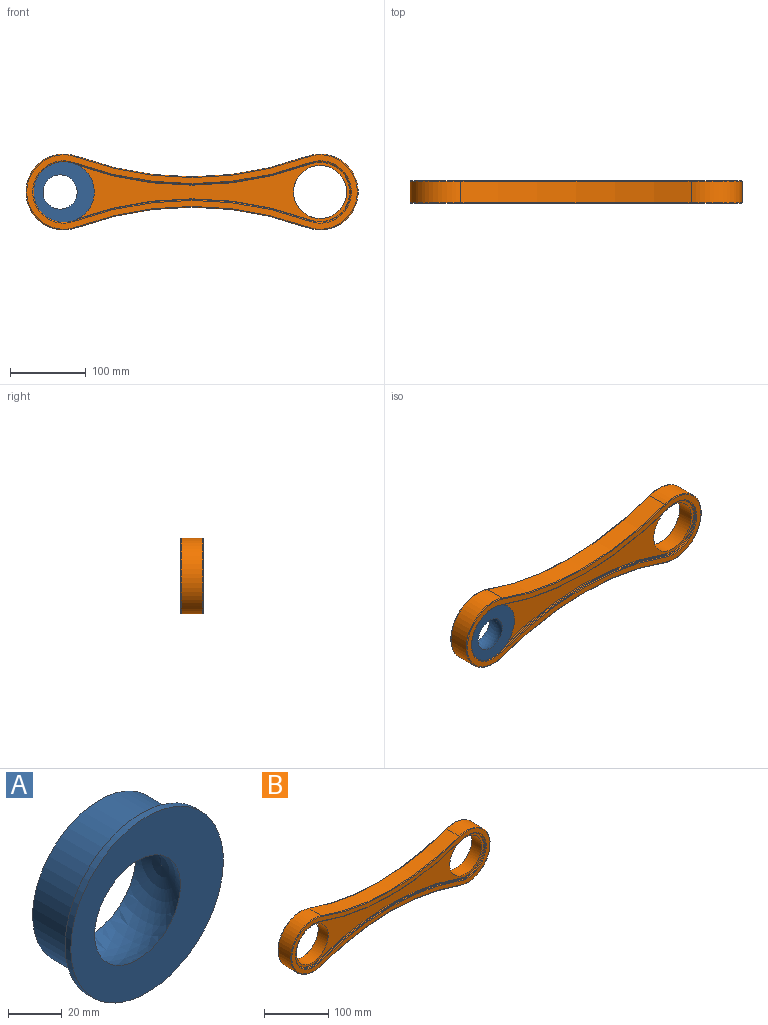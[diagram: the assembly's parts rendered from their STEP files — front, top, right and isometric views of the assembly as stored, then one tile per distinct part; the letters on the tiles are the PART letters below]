
ASSEMBLY  parts=2 mates=1
PART A: 6 faces, bbox 80x53x80 mm
  f0: plane 70x70mm, normal (0,1,0), area 2022.4mm2, adj f1,f5
  f1: cylinder r=35mm len=70mm, axis (0,1,0), area 4838.1mm2, adj f0,f2
  f2: plane 80x80mm, normal (0,1,0), area 1178.1mm2, adj f1,f3
  f3: cylinder r=40mm len=80mm, axis (0,1,0), area 754mm2, adj f2,f4
  f4: plane 80x80mm, normal (0,-1,0), area 3436.1mm2, adj f3,f5
  f5: sphere r=26.5mm, area 4163.4mm2, adj f0,f4
PART B: 42 faces, bbox 445.7x30x108.2 mm
  f0: cylinder r=35mm len=70mm, axis (0,1,0), area 4838.1mm2, adj f12,f17
  f1: cylinder r=35mm len=70mm, axis (0,1,0), area 4838.1mm2, adj f12,f17
  f2: plane 435.5x98mm, normal (0,1,0), area 7775mm2, adj f26,f27,f28,f29,f34,f35,f36,f37
  f3: plane 435.5x98mm, normal (0,-1,0), area 7775mm2, adj f30,f31,f32,f33,f38,f39,f40,f41
  f4: cylinder r=439.61mm len=303.03mm, axis (0,1,0), area 8662.6mm2, adj f5,f7,f36,f40
  f5: cylinder r=50mm len=100mm, axis (0,1,0), area 5383.5mm2, adj f4,f6,f34,f38
  f6: cylinder r=439.61mm len=303.03mm, axis (0,1,0), area 8662.6mm2, adj f5,f7,f35,f39
  f7: cylinder r=50mm len=100mm, axis (0,1,0), area 5383.5mm2, adj f4,f6,f37,f41
  f8: cylinder r=449.61mm len=309.93mm, axis (0,-1,0), area 632.8mm2, adj f9,f11,f24,f30
  f9: cylinder r=40mm len=80mm, axis (0,-1,0), area 307.6mm2, adj f8,f10,f22,f31
  f10: cylinder r=449.61mm len=309.93mm, axis (0,-1,0), area 632.8mm2, adj f9,f11,f23,f33
  f11: cylinder r=40mm len=80mm, axis (0,-1,0), area 307.6mm2, adj f8,f10,f25,f32
  f12: plane 415.5x78mm, normal (0,-1,0), area 10372.7mm2, adj f0,f1,f22,f23,f24,f25
  f13: cylinder r=449.61mm len=309.93mm, axis (0,1,0), area 632.8mm2, adj f14,f16,f20,f26
  f14: cylinder r=40mm len=80mm, axis (0,1,0), area 307.6mm2, adj f13,f15,f21,f28
  f15: cylinder r=449.61mm len=309.93mm, axis (0,1,0), area 632.8mm2, adj f14,f16,f19,f29
  f16: cylinder r=40mm len=80mm, axis (0,1,0), area 307.6mm2, adj f13,f15,f18,f27
  f17: plane 415.5x78mm, normal (0,1,0), area 10372.7mm2, adj f0,f1,f18,f19,f20,f21
  f18: torus R=39mm, axis (0,1,0), area 239.4mm2, adj f16,f17,f19,f20
  f19: torus R=450.61mm, axis (0,1,0), area 497.4mm2, adj f15,f17,f18,f21
  f20: torus R=450.61mm, axis (0,1,0), area 497.4mm2, adj f13,f17,f18,f21
  f21: torus R=39mm, axis (0,1,0), area 239.4mm2, adj f14,f17,f19,f20
  f22: torus R=39mm, axis (0,-1,0), area 239.4mm2, adj f9,f12,f23,f24
  f23: torus R=450.61mm, axis (0,-1,0), area 497.4mm2, adj f10,f12,f22,f25
  f24: torus R=450.61mm, axis (0,-1,0), area 497.4mm2, adj f8,f12,f22,f25
  f25: torus R=39mm, axis (0,-1,0), area 239.4mm2, adj f11,f12,f23,f24
  f26: torus R=448.61mm, axis (0,-1,0), area 496.6mm2, adj f2,f13,f27,f28
  f27: torus R=41mm, axis (0,-1,0), area 243.8mm2, adj f2,f16,f26,f29
  f28: torus R=41mm, axis (0,-1,0), area 243.8mm2, adj f2,f14,f26,f29
  f29: torus R=448.61mm, axis (0,-1,0), area 496.6mm2, adj f2,f15,f27,f28
  f30: torus R=448.61mm, axis (0,-1,0), area 496.6mm2, adj f3,f8,f31,f32
  f31: torus R=41mm, axis (0,-1,0), area 243.8mm2, adj f3,f9,f30,f33
  f32: torus R=41mm, axis (0,-1,0), area 243.8mm2, adj f3,f11,f30,f33
  f33: torus R=448.61mm, axis (0,-1,0), area 496.6mm2, adj f3,f10,f31,f32
  f34: torus R=49mm, axis (0,-1,0), area 299.8mm2, adj f2,f5,f35,f36
  f35: torus R=440.61mm, axis (0,-1,0), area 486.4mm2, adj f2,f6,f34,f37
  f36: torus R=440.61mm, axis (0,-1,0), area 486.4mm2, adj f2,f4,f34,f37
  f37: torus R=49mm, axis (0,-1,0), area 299.8mm2, adj f2,f7,f35,f36
  f38: torus R=49mm, axis (0,-1,0), area 299.8mm2, adj f3,f5,f39,f40
  f39: torus R=440.61mm, axis (0,-1,0), area 486.4mm2, adj f3,f6,f38,f41
  f40: torus R=440.61mm, axis (0,-1,0), area 486.4mm2, adj f3,f4,f38,f41
  f41: torus R=49mm, axis (0,-1,0), area 299.8mm2, adj f3,f7,f39,f40
PLACE A t=(-171.52,0.77,0.69)mm
PLACE B t=(-2.77,0.77,0.69)mm fixed
MATE fastened B.f0 <-> A.f1  axis (0,1,0) through (-171.52,0.77,0.69)mm
